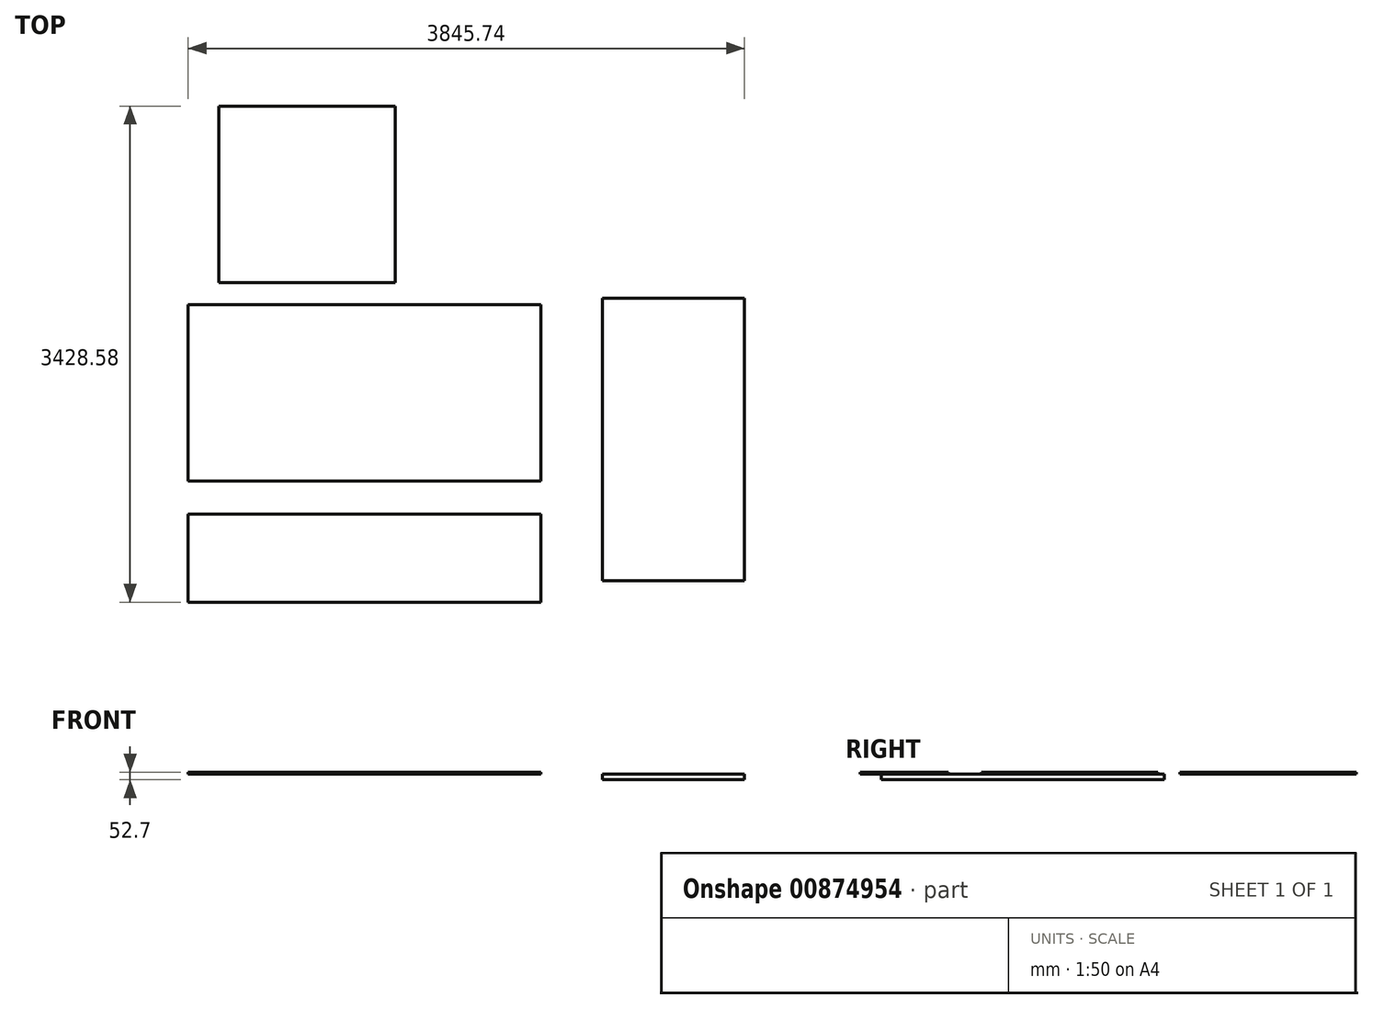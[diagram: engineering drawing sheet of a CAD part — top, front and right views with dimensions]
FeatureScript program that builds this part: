
annotation { "Feature Type Name" : "Feature", "Feature Type Description" : "" }
export const myFeature = defineFeature(function(context is Context, id is Id, definition is map)
    precondition{}
    {
        {
            var Q0;
            Q0=qCreatedBy(makeId("Top.planeOp"),FACE);
            var sketch = newSketch(context, id + "F0", { "sketchPlane" : qUnion([Q0])});
            skLineSegment(sketch, "E0.bottom", {"start": v(-1001.1, 600.28) * mm, "end": v(1437.3, 600.28) * mm});
            skLineSegment(sketch, "E0.top", {"start": v(-1001.1, -618.92) * mm, "end": v(1437.3, -618.92) * mm});
            skLineSegment(sketch, "E0.left", {"start": v(-1001.1, 600.28) * mm, "end": v(-1001.1, -618.92) * mm});
            skLineSegment(sketch, "E0.right", {"start": v(1437.3, 600.28) * mm, "end": v(1437.3, -618.92) * mm});
            skLineSegment(sketch, "E1.bottom", {"start": v(-790.56, 1971.84) * mm, "end": v(428.64, 1971.84) * mm});
            skLineSegment(sketch, "E1.top", {"start": v(-790.56, 752.64) * mm, "end": v(428.64, 752.64) * mm});
            skLineSegment(sketch, "E1.left", {"start": v(-790.56, 1971.84) * mm, "end": v(-790.56, 752.64) * mm});
            skLineSegment(sketch, "E1.right", {"start": v(428.64, 1971.84) * mm, "end": v(428.64, 752.64) * mm});
            skSolve(sketch);
        }
        {
            var Q0;
            Q0 = qSketchRegion(id + "F0", true);
            extrude(context, id + "F1", {"entities" : qUnion([Q0]), "depth" : 12.7 * mm, "offsetDistance" : 25.4 * mm});
        }
        {
            var Q0;
            Q0=qCreatedBy(makeId("Top.planeOp"),FACE);
            var sketch = newSketch(context, id + "F2", { "sketchPlane" : qUnion([Q0])});
            skLineSegment(sketch, "E2.bottom", {"start": v(-1001.6, -847.14) * mm, "end": v(1436.8, -847.14) * mm});
            skLineSegment(sketch, "E2.top", {"start": v(-1001.6, -1456.74) * mm, "end": v(1436.8, -1456.74) * mm});
            skLineSegment(sketch, "E2.left", {"start": v(-1001.6, -847.14) * mm, "end": v(-1001.6, -1456.74) * mm});
            skLineSegment(sketch, "E2.right", {"start": v(1436.8, -847.14) * mm, "end": v(1436.8, -1456.74) * mm});
            skSolve(sketch);
        }
        {
            var Q0;
            Q0=makeQuery(id+"F2.imprint","IMPRINT",FACE,{"disambiguationData":[TD([[makeQuery(id+"F2.imprint","IMPRINT",EDGE,{"derivedFrom":sQuery(id+"F2.wireOp",EDGE,"E2.bottom")}),-1.0]])]});
            extrude(context, id + "F3", {"entities" : qUnion([Q0]), "depth" : 12.7 * mm, "offsetDistance" : 25.4 * mm});
        }
        {
            var Q0;
            Q0=makeQuery(id+"F1.opExtrude","CAP_FACE",FACE,{"disambiguationData":[OSD([sQuery(id+"F0.wireOp",EDGE,"E0.bottom"),sQuery(id+"F0.wireOp",EDGE,"E0.top"),sQuery(id+"F0.wireOp",EDGE,"E0.left"),sQuery(id+"F0.wireOp",EDGE,"E0.right")])],"isStart":true});
            var sketch = newSketch(context, id + "F4", { "sketchPlane" : qUnion([Q0])});
            skLineSegment(sketch, "E3.bottom", {"start": v(1862.13, -643.54) * mm, "end": v(2844.13, -643.54) * mm});
            skLineSegment(sketch, "E3.top", {"start": v(1862.13, 1310.46) * mm, "end": v(2844.13, 1310.46) * mm});
            skLineSegment(sketch, "E3.left", {"start": v(1862.13, -643.54) * mm, "end": v(1862.13, 1310.46) * mm});
            skLineSegment(sketch, "E3.right", {"start": v(2844.13, -643.54) * mm, "end": v(2844.13, 1310.46) * mm});
            skSolve(sketch);
        }
        {
            var Q0;
            Q0 = qSketchRegion(id + "F4", true);
            extrude(context, id + "F5", {"entities" : qUnion([Q0]), "depth" : 40 * mm, "offsetDistance" : 25.4 * mm});
        }
    });
